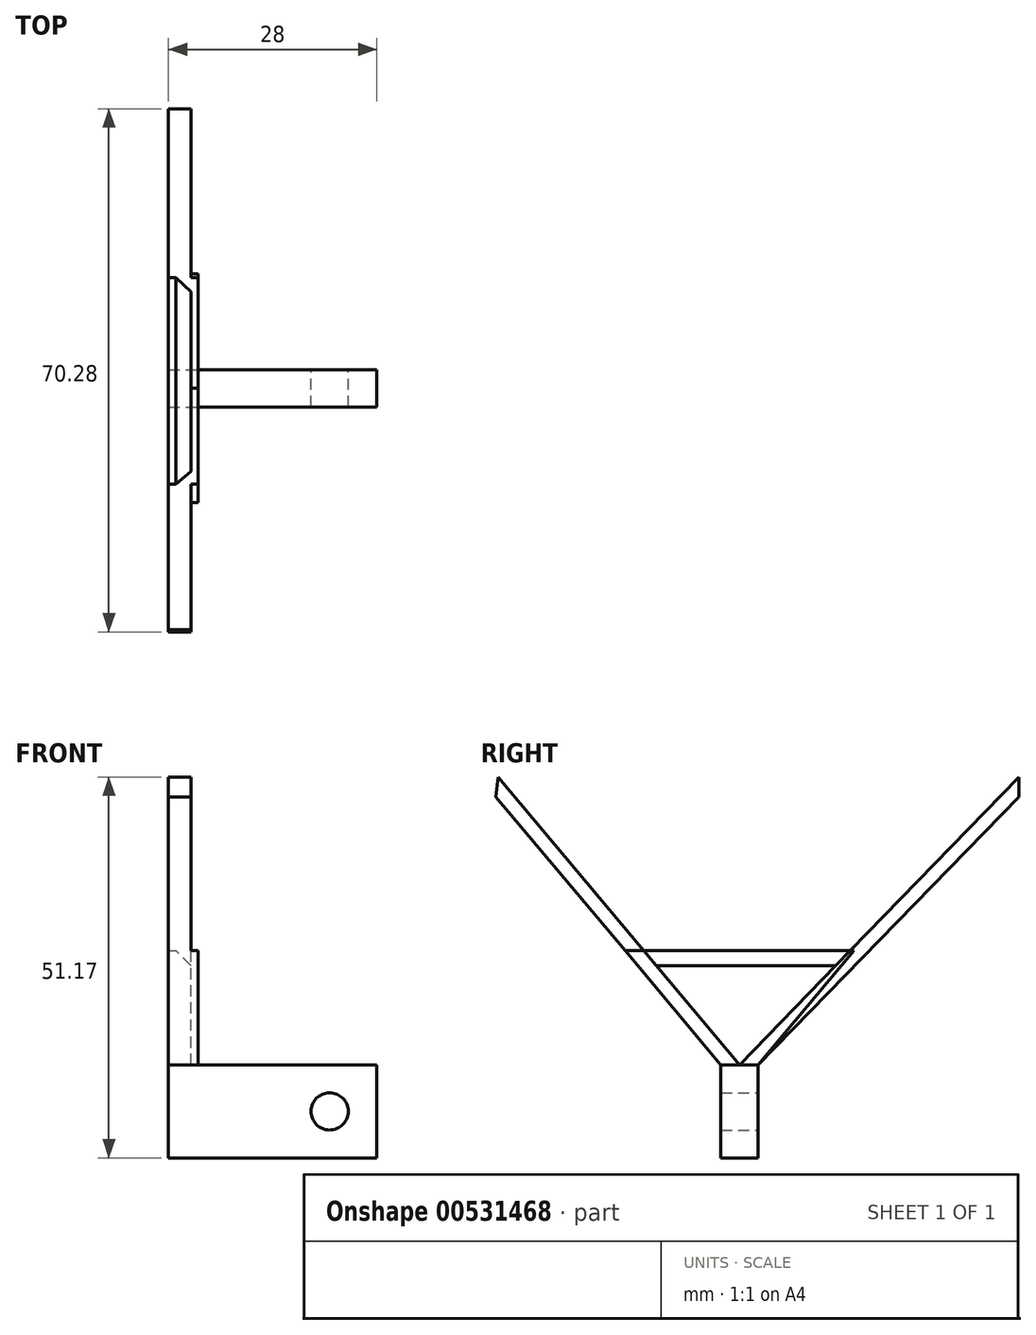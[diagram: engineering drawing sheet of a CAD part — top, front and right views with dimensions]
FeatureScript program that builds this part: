
annotation { "Feature Type Name" : "Feature", "Feature Type Description" : "" }
export const myFeature = defineFeature(function(context is Context, id is Id, definition is map)
    precondition{}
    {
        {
            var Q0;
            Q0=qCreatedBy(makeId("Front.planeOp"),FACE);
            var sketch = newSketch(context, id + "F0", { "sketchPlane" : qUnion([Q0])});
            skLineSegment(sketch, "E0.bottom", {"start": v(-18.65, 6.25) * mm, "end": v(6.35, 6.25) * mm});
            skLineSegment(sketch, "E0.top", {"start": v(-18.65, -6.25) * mm, "end": v(6.35, -6.25) * mm});
            skLineSegment(sketch, "E0.left", {"start": v(-18.65, 6.25) * mm, "end": v(-18.65, -6.25) * mm});
            skLineSegment(sketch, "E0.right", {"start": v(6.35, 6.25) * mm, "end": v(6.35, -6.25) * mm});
            skPoint(sketch, "E0.middle", {"position": v(0, 0) * mm});
            skCircle(sketch, "E1", {"center": v(0, 0) * mm, "radius": 2.5 * mm});
            skSolve(sketch);
        }
        {
            var Q0;
            Q0 = qSketchRegion(id + "F0", true);
            extrude(context, id + "F1", {"entities" : qUnion([Q0]), "depth" : 5 * mm, "offsetDistance" : 25.4 * mm});
        }
        {
            var Q0;
            Q0=makeQuery(id+"F1.opExtrude","SWEPT_FACE",FACE,{"disambiguationData":[OSD([sQuery(id+"F0.wireOp",EDGE,"E0.left")])]});
            var sketch = newSketch(context, id + "F2", { "sketchPlane" : qUnion([Q0])});
            skLineSegment(sketch, "E2.bottom", {"start": v(0, -6.25) * mm, "end": v(5, -6.25) * mm});
            skLineSegment(sketch, "E2.top", {"start": v(0, 6.25) * mm, "end": v(5, 6.25) * mm});
            skLineSegment(sketch, "E2.left", {"start": v(0, -6.25) * mm, "end": v(0, 6.25) * mm});
            skLineSegment(sketch, "E2.right", {"start": v(5, -6.25) * mm, "end": v(5, 6.25) * mm});
            skLineSegment(sketch, "E3", {"start": v(0, 6.25) * mm, "end": v(-12.86, 21.57) * mm});
            skLineSegment(sketch, "E4", {"start": v(-12.86, 21.57) * mm, "end": v(17.86, 21.57) * mm});
            skLineSegment(sketch, "E5", {"start": v(17.86, 21.57) * mm, "end": v(5, 6.25) * mm});
            skLineSegment(sketch, "E6", {"start": v(5, 6.25) * mm, "end": v(35.23, 42.27) * mm});
            skLineSegment(sketch, "E7", {"start": v(2.5, 6.25) * mm, "end": v(34.95, 44.92) * mm});
            skLineSegment(sketch, "E8", {"start": v(34.95, 44.92) * mm, "end": v(35.23, 42.27) * mm});
            skLineSegment(sketch, "E9", {"start": v(0, 6.25) * mm, "end": v(-35.02, 42.27) * mm});
            skLineSegment(sketch, "E10", {"start": v(2.5, 6.25) * mm, "end": v(-35.05, 44.88) * mm});
            skLineSegment(sketch, "E11", {"start": v(-35.05, 44.88) * mm, "end": v(-35.02, 42.27) * mm});
            skSolve(sketch);
        }
        {
            var Q0;
            Q0=makeQuery(id+"F2.imprint","IMPRINT",FACE,{"disambiguationData":[TD([[makeQuery(id+"F2.imprint","IMPRINT",EDGE,{"derivedFrom":sQuery(id+"F2.wireOp",EDGE,"E2.bottom")}),-1.0]])]});
            var Q1;
            Q1=makeQuery(id+"F2.imprint","IMPRINT",FACE,{"disambiguationData":[TD([[makeQuery(id+"F2.imprint","IMPRINT",EDGE,{"derivedFrom":sQuery(id+"F2.wireOp",EDGE,"E2.top")}),-1.0]])]});
            extrude(context, id + "F3", {"entities" : qUnion([Q0, Q1]), "operationType" : NewBodyOperationType.ADD, "oppositeDirection" : true, "depth" : 1 * mm, "offsetDistance" : 25 * mm});
        }
        {
            var Q0;
            Q0 = qSketchRegion(id + "F2", true);
            extrude(context, id + "F4", {"entities" : qUnion([Q0]), "operationType" : NewBodyOperationType.ADD, "depth" : 3 * mm, "offsetDistance" : 25 * mm});
        }
        {
            var Q0;
            Q0=makeQuery(id+"F4.opExtrude","CAP_EDGE",EDGE,{"disambiguationData":[OSD([sQuery(id+"F2.wireOp",EDGE,"E4")])],"isStart":true});
            chamfer(context, id + "F5", {"entities" : qUnion([Q0]), "width" : 2 * mm, "tangentPropagation" : true});
        }
    });
